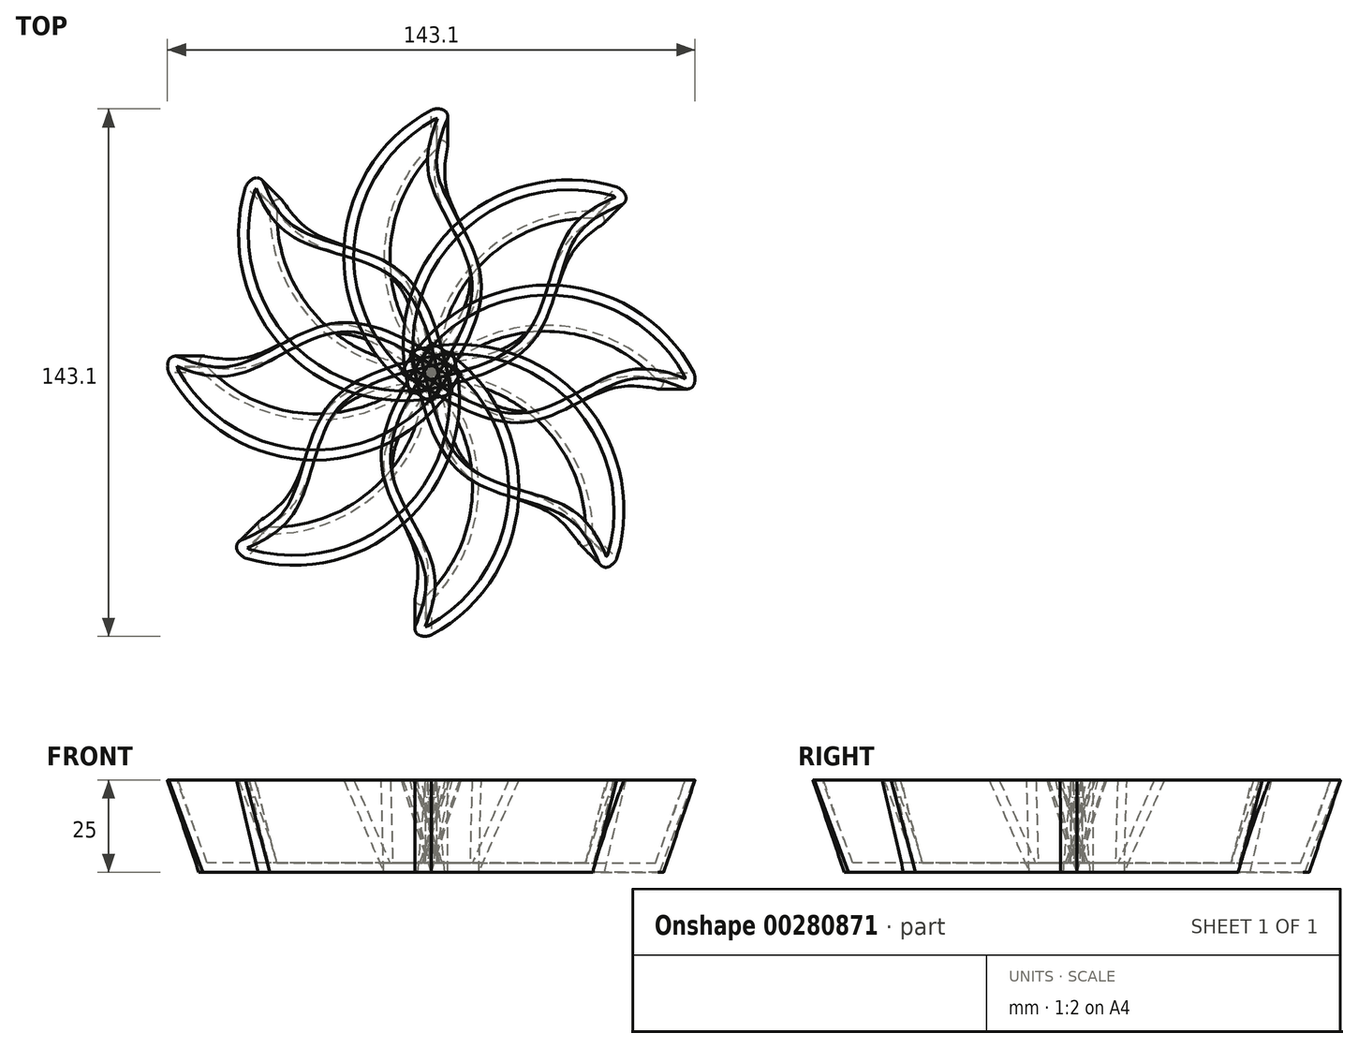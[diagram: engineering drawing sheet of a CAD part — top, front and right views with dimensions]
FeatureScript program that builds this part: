
annotation { "Feature Type Name" : "Feature", "Feature Type Description" : "" }
export const myFeature = defineFeature(function(context is Context, id is Id, definition is map)
    precondition{}
    {
        {
            var Q0;
            Q0=qCreatedBy(makeId("Top.planeOp"),FACE);
            var sketch = newSketch(context, id + "F0", { "sketchPlane" : qUnion([Q0])});
            skArc(sketch, "E0", {"start": v(0, 61.93) * mm, "mid": v(-12.83, 30.97) * mm, "end": v(0, 0) * mm});
            skFitSpline(sketch, "E1", {"points": [v(0, 0) * mm, v(12.94, 25.71) * mm, v(4.53, 48.35) * mm, v(4.53, 61.93) * mm], "startDerivative": vector(51.7, 66.62) * mm, "endDerivative": vector(8.66, 48.65) * mm});
            skArc(sketch, "E2", {"start": v(4.1, 62.38) * mm, "mid": v(1.96, 63.04) * mm, "end": v(0, 61.93) * mm});
            skArc(sketch, "E3.filletArc", {"start": v(4.44, 61.45) * mm, "mid": v(4.4, 61.96) * mm, "end": v(4.1, 62.38) * mm});
            skSolve(sketch);
        }
        {
            var Q0;
            Q0=qCreatedBy(makeId("Top.planeOp"),FACE);
            cPlane(context, id + "F1", {"entities" : qUnion([Q0]), "cplaneType" : CPlaneType.OFFSET, "offset" : 25 * mm, "width" : 150 * mm, "height" : 150 * mm});
        }
        {
            var Q0;
            Q0=qCreatedBy(id+"F1.planeOp",FACE);
            var sketch = newSketch(context, id + "F2", { "sketchPlane" : qUnion([Q0])});
            skArc(sketch, "E4", {"start": v(0, 71.22) * mm, "mid": v(-23.74, 31.57) * mm, "end": v(0, -8.08) * mm});
            skFitSpline(sketch, "E5", {"points": [v(0, -8.08) * mm, v(13.43, 25.83) * mm, v(1.95, 53.26) * mm, v(4.95, 70.22) * mm], "startDerivative": vector(57.38, 89.24) * mm, "endDerivative": vector(25.24, 61) * mm});
            skArc(sketch, "E6", {"start": v(3.04, 71.35) * mm, "mid": v(1.5, 71.54) * mm, "end": v(0, 71.22) * mm});
            skArc(sketch, "E7.filletArc", {"start": v(4.31, 68.69) * mm, "mid": v(4.27, 70.3) * mm, "end": v(3.04, 71.35) * mm});
            skSolve(sketch);
        }
        {
            var Q0;
            Q0=makeQuery(id+"F0.imprint","IMPRINT",FACE,{"disambiguationData":[TD([[makeQuery(id+"F0.imprint","IMPRINT",EDGE,{"derivedFrom":sQuery(id+"F0.wireOp",EDGE,"E0")}),1.0]])]});
            var Q1;
            Q1=makeQuery(id+"F2.imprint","IMPRINT",FACE,{"disambiguationData":[TD([[makeQuery(id+"F2.imprint","IMPRINT",EDGE,{"derivedFrom":sQuery(id+"F2.wireOp",EDGE,"E4")}),1.0]])]});
            loft(context, id + "F3", {"sheetProfilesArray" : [{ "sheetProfileEntities" : qUnion([Q0]) }, { "sheetProfileEntities" : qUnion([Q1]) }]});
        }
        {
            var Q0;
            Q0=makeQuery(id+"F3.opLoft","CAP_FACE",FACE,{"disambiguationData":[OSD([makeQuery(id+"F2.imprint","IMPRINT",FACE,{"disambiguationData":[TD([[makeQuery(id+"F2.imprint","IMPRINT",EDGE,{"derivedFrom":sQuery(id+"F2.wireOp",EDGE,"E4")}),1.0]])]})])],"isStart":true});
            shell(context, id + "F4", {"entities" : qUnion([Q0]), "thickness" : 2.5 * mm});
        }
        {
            var Q0;
            Q0=qCreatedBy(makeId("Top.planeOp"),FACE);
            var sketch = newSketch(context, id + "F5", { "sketchPlane" : qUnion([Q0])});
            skCircle(sketch, "E8", {"center": v(0, 0) * mm, "radius": 8.02 * mm});
            skSolve(sketch);
        }
        {
            var Q0;
            Q0=sQuery(id+"F5.wireOp",EDGE,"E8");
            extrude(context, id + "F6", {"bodyType" : ToolBodyType.SURFACE, "surfaceEntities" : qUnion([Q0]), "depth" : 25 * mm});
        }
        {
            var Q0;
            Q0=makeQuery(id+"F3.opLoft","SWEPT_BODY",BODY,{"disambiguationData":[OSD([makeQuery(id+"F0.imprint","IMPRINT",FACE,{"disambiguationData":[TD([[makeQuery(id+"F0.imprint","IMPRINT",EDGE,{"derivedFrom":sQuery(id+"F0.wireOp",EDGE,"E0")}),1.0]])]}),makeQuery(id+"F2.imprint","IMPRINT",FACE,{"disambiguationData":[TD([[makeQuery(id+"F2.imprint","IMPRINT",EDGE,{"derivedFrom":sQuery(id+"F2.wireOp",EDGE,"E4")}),1.0]])]})])]});
            var Q1;
            Q1=makeQuery(id+"F6.opExtrude","CAP_EDGE",EDGE,{"disambiguationData":[OSD([sQuery(id+"F5.wireOp",EDGE,"E8")])],"isStart":false});
            circularPattern(context, id + "F7", {"entities" : qUnion([Q0]), "axis" : qUnion([Q1]), "angle" : 360 * degree, "instanceCount" : 8, "oppositeDirection" : true, "equalSpace" : true});
        }
    });
